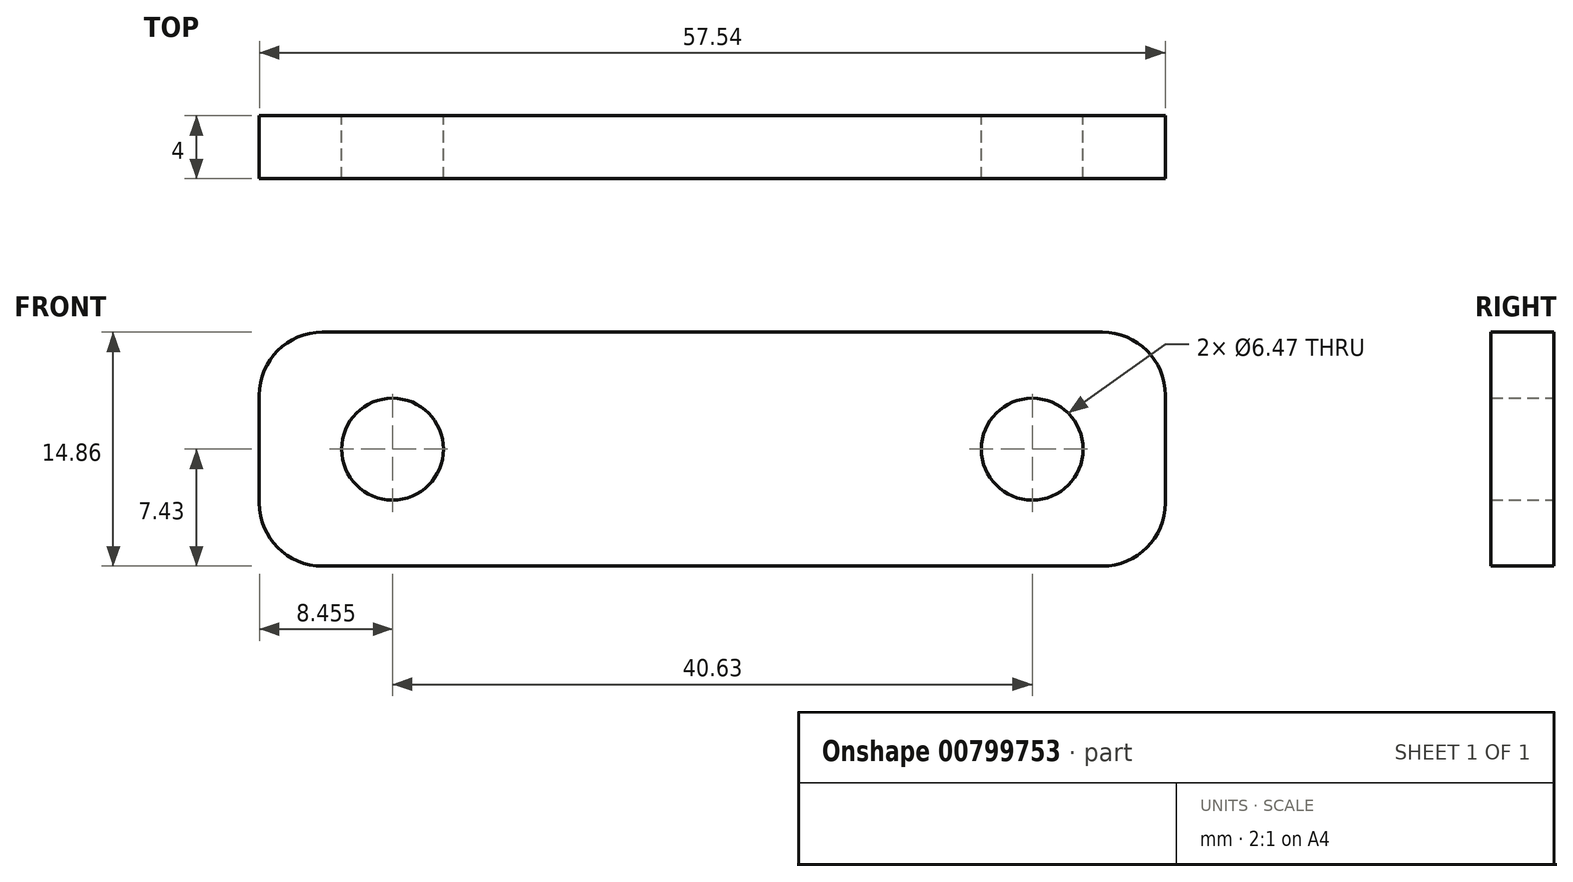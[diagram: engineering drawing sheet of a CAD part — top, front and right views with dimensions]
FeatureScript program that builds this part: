
annotation { "Feature Type Name" : "Feature", "Feature Type Description" : "" }
export const myFeature = defineFeature(function(context is Context, id is Id, definition is map)
    precondition{}
    {
        {
            var Q0;
            Q0=qCreatedBy(makeId("Front.planeOp"),FACE);
            var sketch = newSketch(context, id + "F0", { "sketchPlane" : qUnion([Q0])});
            skLineSegment(sketch, "E0.bottom", {"start": v(28.78, 7.43) * mm, "end": v(-28.78, 7.43) * mm});
            skLineSegment(sketch, "E0.top", {"start": v(28.78, -7.43) * mm, "end": v(-28.78, -7.43) * mm});
            skLineSegment(sketch, "E0.left", {"start": v(28.78, 7.43) * mm, "end": v(28.78, -7.43) * mm});
            skLineSegment(sketch, "E0.right", {"start": v(-28.78, 7.43) * mm, "end": v(-28.78, -7.43) * mm});
            skPoint(sketch, "E0.middle", {"position": v(0, 0) * mm});
            skCircle(sketch, "E1", {"center": v(-20.32, 0) * mm, "radius": 3.23 * mm});
            skPoint(sketch, "E1.centerSnap0", {"position": v(-28.78, 0) * mm});
            skCircle(sketch, "E2", {"center": v(20.32, 0) * mm, "radius": 3.23 * mm});
            skSolve(sketch);
        }
        {
            var Q0;
            Q0=makeQuery(id+"F0.imprint","IMPRINT",FACE,{"disambiguationData":[TD([[makeQuery(id+"F0.imprint","IMPRINT",EDGE,{"derivedFrom":sQuery(id+"F0.wireOp",EDGE,"E0.bottom")}),1.0]])]});
            extrude(context, id + "F1", {"entities" : qUnion([Q0]), "depth" : 4 * mm, "offsetDistance" : 25 * mm});
        }
        {
            var Q0;
            Q0=makeQuery(id+"F1.opExtrude","SWEPT_EDGE",EDGE,{"disambiguationData":[OSD([sQuery(id+"F0.wireOp",EDGE,"E0.top"),sQuery(id+"F0.wireOp",EDGE,"E0.left")])]});
            var Q1;
            Q1=makeQuery(id+"F1.opExtrude","SWEPT_EDGE",EDGE,{"disambiguationData":[OSD([sQuery(id+"F0.wireOp",EDGE,"E0.bottom"),sQuery(id+"F0.wireOp",EDGE,"E0.left")])]});
            var Q2;
            Q2=makeQuery(id+"F1.opExtrude","SWEPT_EDGE",EDGE,{"disambiguationData":[OSD([sQuery(id+"F0.wireOp",EDGE,"E0.top"),sQuery(id+"F0.wireOp",EDGE,"E0.right")])]});
            var Q3;
            Q3=makeQuery(id+"F1.opExtrude","SWEPT_EDGE",EDGE,{"disambiguationData":[OSD([sQuery(id+"F0.wireOp",EDGE,"E0.bottom"),sQuery(id+"F0.wireOp",EDGE,"E0.right")])]});
            fillet(context, id + "F2", {"entities" : qUnion([Q0, Q1, Q2, Q3]), "radius" : 4 * mm, "tangentPropagation" : true, "allowEdgeOverflow" : false});
        }
    });
